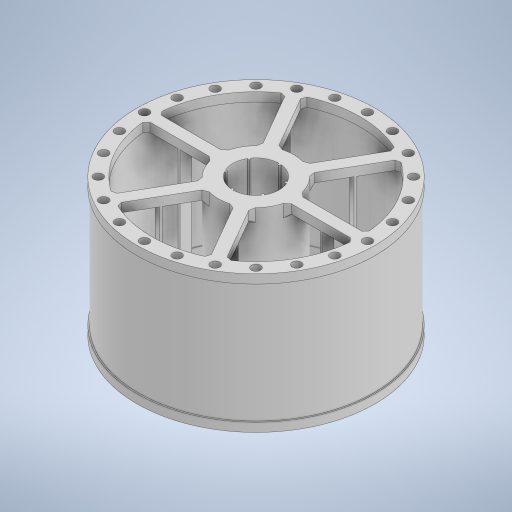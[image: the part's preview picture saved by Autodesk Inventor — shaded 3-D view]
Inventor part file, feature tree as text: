
AUTODESK INVENTOR PART (.ipt)
format: ipt  version: 2024 (Build 280153000, 153)  size: 592,384 bytes
history: native  units: mm
features: extrude x7, sketch x7, pattern_circular x4, chamfer x2, mirror x2, fillet x1
ambient origin geometry x8: Origin, YZ Plane, XZ Plane, XY Plane, X Axis, Y Axis, Z Axis, Center Point
bodies: Volumenkörper1 (feature_tree)
feature tree (23):
  extrude  "Extrusion1"  Depth=25.5mm
  extrude  "Extrusion2"  Depth=70.0mm
  extrude  "Extrusion4"  Depth=3.0mm TaperAngle=0.0deg
  chamfer  "Fasen1"  Distance=3.0mm
  mirror  "Spiegeln2"
  pattern_circular  "Runde Anordnung2"  Count=6 Angle=360.0deg
  chamfer  "Fasen2"  Distance=1.25mm Angle=45.0deg
  extrude  "Extrusion5"  Depth=40.2mm TaperAngle=0.0deg
  pattern_circular  "Runde Anordnung3"  Count=24 Angle=360.0deg
  mirror  "Spiegeln3"
  extrude  "Extrusion6"  Depth=40.2mm
  pattern_circular  "Runde Anordnung4"  [2 undecoded]
  fillet  "Rundung1"  Radius=46.2mm
  extrude  "Extrusion7"  Depth=40.2mm TaperAngle=360.0deg
  extrude  "Extrusion8"  Depth=40.2mm
  pattern_circular  "Runde Anordnung5"  [2 undecoded]
  sketch  "Skizze1"  dims[d2=15.5mm d3=25.5mm]
  sketch  "Skizze3"  dims[d4=46.2mm d5=0.0mm d6=70.0mm]
  sketch  "Skizze4"  dims[d7=80.0mm d8=3.0mm d9=0.0mm]
  sketch  "Skizze5"  dims[d13=0.3mm]
  sketch  "Skizze6"  dims[d21=2.0mm d22=3.0mm d23=0.0mm]
  sketch  "Skizze7"  dims[d24=1.25mm d25=2.0mm d26=45.0deg d27=60.0mm d28=360.0deg d30=1.25mm d31=2.0mm d32=45.0deg]
  sketch  "Skizze8"  dims[d33=3.0mm d34=3.0mm d35=0.0mm d36=240.0mm d37=360.0deg d39=0.63mm d40=0.75mm d41=46.2mm d42=0.0mm d43=60.0mm d44=360.0deg d46=0.35mm d47=79.18mm d48=78.5mm d49=40.2mm d50=0.0mm d51=70.5mm d52=71.18mm d53=0.5mm d54=0.68mm d55=40.2mm d56=0.0mm d57=60.0mm d58=360.0deg]
note: 4 required parameter values undecoded (feature->parameter linkage not recoverable at this tier; creation-order binding heuristic only, values carry confidence <= 0.55)
